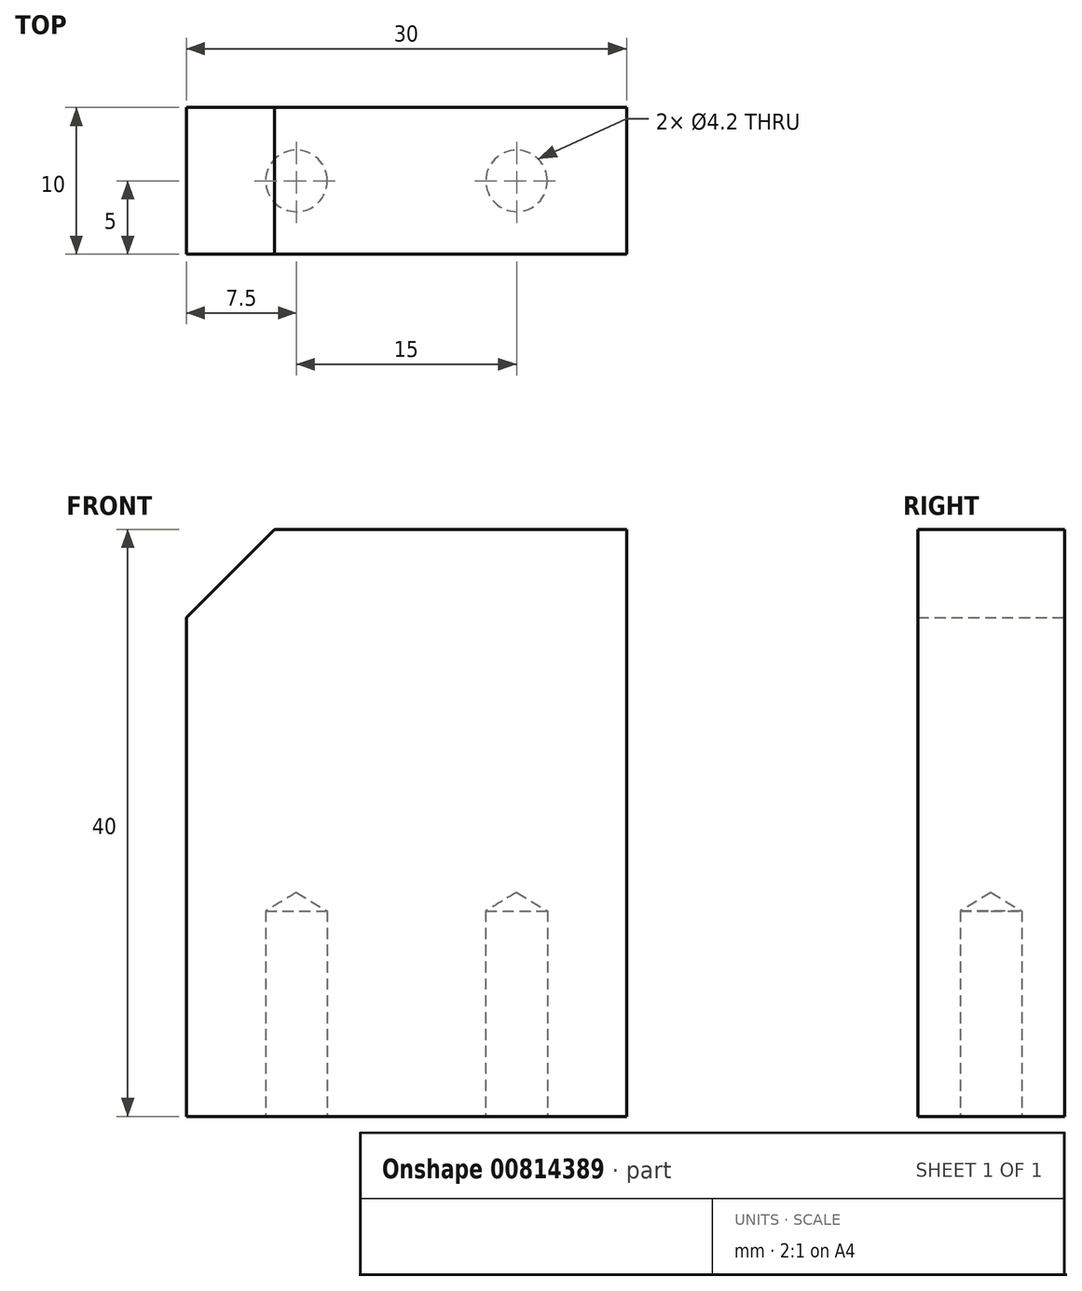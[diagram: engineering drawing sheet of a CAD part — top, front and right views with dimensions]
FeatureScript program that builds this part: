
annotation { "Feature Type Name" : "Feature", "Feature Type Description" : "" }
export const myFeature = defineFeature(function(context is Context, id is Id, definition is map)
    precondition{}
    {
        {
            var Q0;
            Q0=qCreatedBy(makeId("Front.planeOp"),FACE);
            var sketch = newSketch(context, id + "F0", { "sketchPlane" : qUnion([Q0])});
            skLineSegment(sketch, "E0.bottom", {"start": v(15, 20) * mm, "end": v(-15, 20) * mm});
            skLineSegment(sketch, "E0.top", {"start": v(15, -20) * mm, "end": v(-15, -20) * mm});
            skLineSegment(sketch, "E0.left", {"start": v(15, 20) * mm, "end": v(15, -20) * mm});
            skLineSegment(sketch, "E0.right", {"start": v(-15, 20) * mm, "end": v(-15, -20) * mm});
            skPoint(sketch, "E0.middle", {"position": v(0, 0) * mm});
            skSolve(sketch);
        }
        {
            var Q0;
            Q0=makeQuery(id+"F0.imprint","IMPRINT",FACE,{"disambiguationData":[TD([[makeQuery(id+"F0.imprint","IMPRINT",EDGE,{"derivedFrom":sQuery(id+"F0.wireOp",EDGE,"E0.bottom")}),1.0]])]});
            extrude(context, id + "F1", {"entities" : qUnion([Q0]), "depth" : 10 * mm, "offsetDistance" : 25 * mm});
        }
        {
            var Q0;
            Q0=makeQuery(id+"F1.opExtrude","SWEPT_EDGE",EDGE,{"disambiguationData":[OSD([sQuery(id+"F0.wireOp",EDGE,"E0.bottom"),sQuery(id+"F0.wireOp",EDGE,"E0.right")])]});
            chamfer(context, id + "F2", {"entities" : qUnion([Q0]), "width" : 6 * mm, "tangentPropagation" : true});
        }
        {
            var Q0;
            Q0=makeQuery(id+"F1.opExtrude","SWEPT_FACE",FACE,{"disambiguationData":[OSD([sQuery(id+"F0.wireOp",EDGE,"E0.top")])]});
            var sketch = newSketch(context, id + "F3", { "sketchPlane" : qUnion([Q0])});
            skLineSegment(sketch, "E1", {"start": v(-7.5, 10) * mm, "end": v(-7.5, 0) * mm});
            skLineSegment(sketch, "E2", {"start": v(7.5, 10) * mm, "end": v(7.5, 0) * mm});
            skPoint(sketch, "E3", {"position": v(-7.5, 5) * mm});
            skPoint(sketch, "E4", {"position": v(7.5, 5) * mm});
            skSolve(sketch);
        }
        {
            var Q0;
            Q0=sQuery(id+"F3.wireOp",VERTEX,"E4");
            var Q1;
            Q1=sQuery(id+"F3.wireOp",VERTEX,"E3");
            var Q2;
            Q2=makeQuery(id+"F1.opExtrude","SWEPT_BODY",BODY,{"disambiguationData":[OSD([sQuery(id+"F0.wireOp",EDGE,"E0.bottom"),sQuery(id+"F0.wireOp",EDGE,"E0.top"),sQuery(id+"F0.wireOp",EDGE,"E0.left"),sQuery(id+"F0.wireOp",EDGE,"E0.right")])]});
            hole(context, id + "F4", {"style" : HoleStyle.SIMPLE, "endStyle" : HoleEndStyle.BLIND, "holeDiameter" : 4.2 * mm, "majorDiameter" : 5 * mm, "holeDepth" : 14 * mm, "isTappedThrough" : true, "tappedDepth" : 12 * mm, "tapClearance" : 3, "locations" : qUnion([Q0, Q1]), "scope" : qUnion([Q2])});
        }
    });
